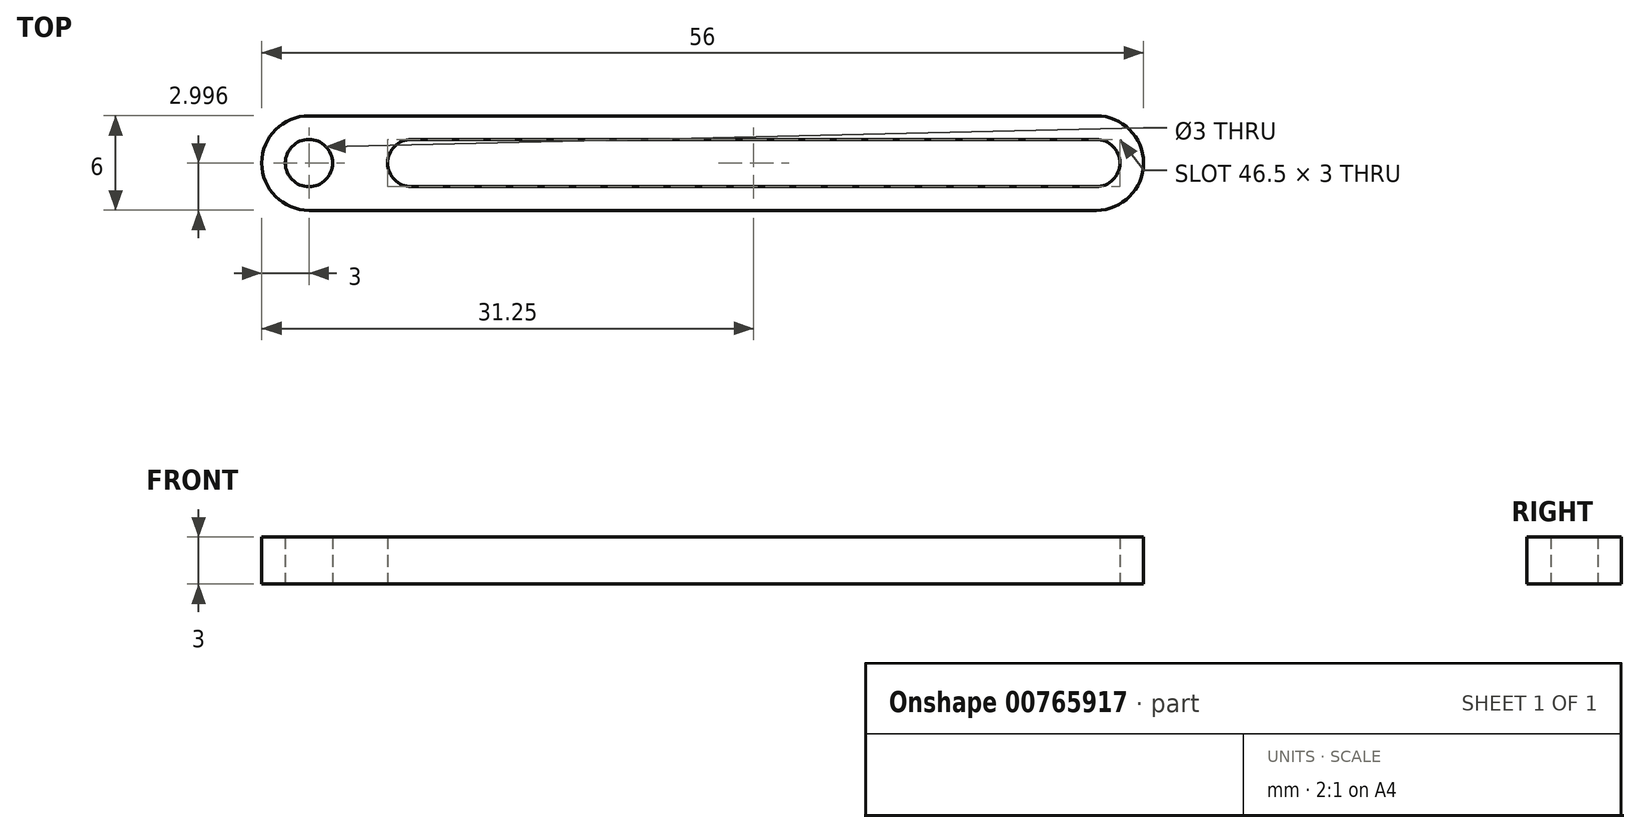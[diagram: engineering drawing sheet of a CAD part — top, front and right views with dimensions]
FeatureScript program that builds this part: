
annotation { "Feature Type Name" : "Feature", "Feature Type Description" : "" }
export const myFeature = defineFeature(function(context is Context, id is Id, definition is map)
    precondition{}
    {
        {
            var Q0;
            Q0=qCreatedBy(makeId("Top.planeOp"),FACE);
            var sketch = newSketch(context, id + "F0", { "sketchPlane" : qUnion([Q0])});
            skLineSegment(sketch, "E0", {"start": v(0, 0) * mm, "end": v(0, 26.48) * mm, "construction": true});
            skLineSegment(sketch, "E1", {"start": v(0, 3.37) * mm, "end": v(-25, 3.37) * mm});
            skCircle(sketch, "E2", {"center": v(-25, 0.37) * mm, "radius": 1.5 * mm});
            skCircle(sketch, "E3", {"center": v(-25, 0.37) * mm, "radius": 3 * mm});
            skCircle(sketch, "E4", {"center": v(-18.5, 0.37) * mm, "radius": 1.5 * mm});
            skLineSegment(sketch, "E5", {"start": v(-25, -2.63) * mm, "end": v(0, -2.63) * mm});
            skLineSegment(sketch, "E6.MirrorCS", {"start": v(25, -2.63) * mm, "end": v(0, -2.63) * mm});
            skCircle(sketch, "E7.MirrorC", {"center": v(25, 0.37) * mm, "radius": 1.5 * mm});
            skLineSegment(sketch, "E8.MirrorCS", {"start": v(0, 3.37) * mm, "end": v(25, 3.37) * mm});
            skArc(sketch, "E9", {"start": v(25, 3.37) * mm, "mid": v(28, 0.37) * mm, "end": v(25, -2.63) * mm});
            skLineSegment(sketch, "E10", {"start": v(-18.5, 1.87) * mm, "end": v(25, 1.87) * mm});
            skLineSegment(sketch, "E11", {"start": v(25, -1.13) * mm, "end": v(-18.5, -1.13) * mm});
            skLineSegment(sketch, "E12", {"start": v(-25, 0.37) * mm, "end": v(-25, -2.63) * mm});
            skLineSegment(sketch, "E13", {"start": v(-18.5, 0.37) * mm, "end": v(-18.5, 0.37) * mm});
            skCircle(sketch, "E14", {"center": v(-13.52, -9.75) * mm, "radius": 5.04 * mm});
            skCircle(sketch, "E15", {"center": v(-13.52, -9.75) * mm, "radius": 3.17 * mm});
            skSolve(sketch);
        }
        {
            var Q0;
            {var subQ5=sQuery(id+"F0.wireOp",EDGE,"E1");Q0=makeQuery(id+"F0.imprint","IMPRINT",FACE,{"disambiguationData":[TD([[makeQuery(id+"F0.imprint","IMPRINT",EDGE,{"derivedFrom":subQ5}),1.0]])]});}
            var Q1;
            Q1=makeQuery(id+"F0.imprint","IMPRINT",FACE,{"disambiguationData":[TD([[makeQuery(id+"F0.imprint","IMPRINT",EDGE,{"derivedFrom":sQuery(id+"F0.wireOp",EDGE,"E2")}),-1.0]])]});
            extrude(context, id + "F1", {"entities" : qUnion([Q0, Q1]), "depth" : 3 * mm, "offsetDistance" : 25 * mm});
        }
    });
